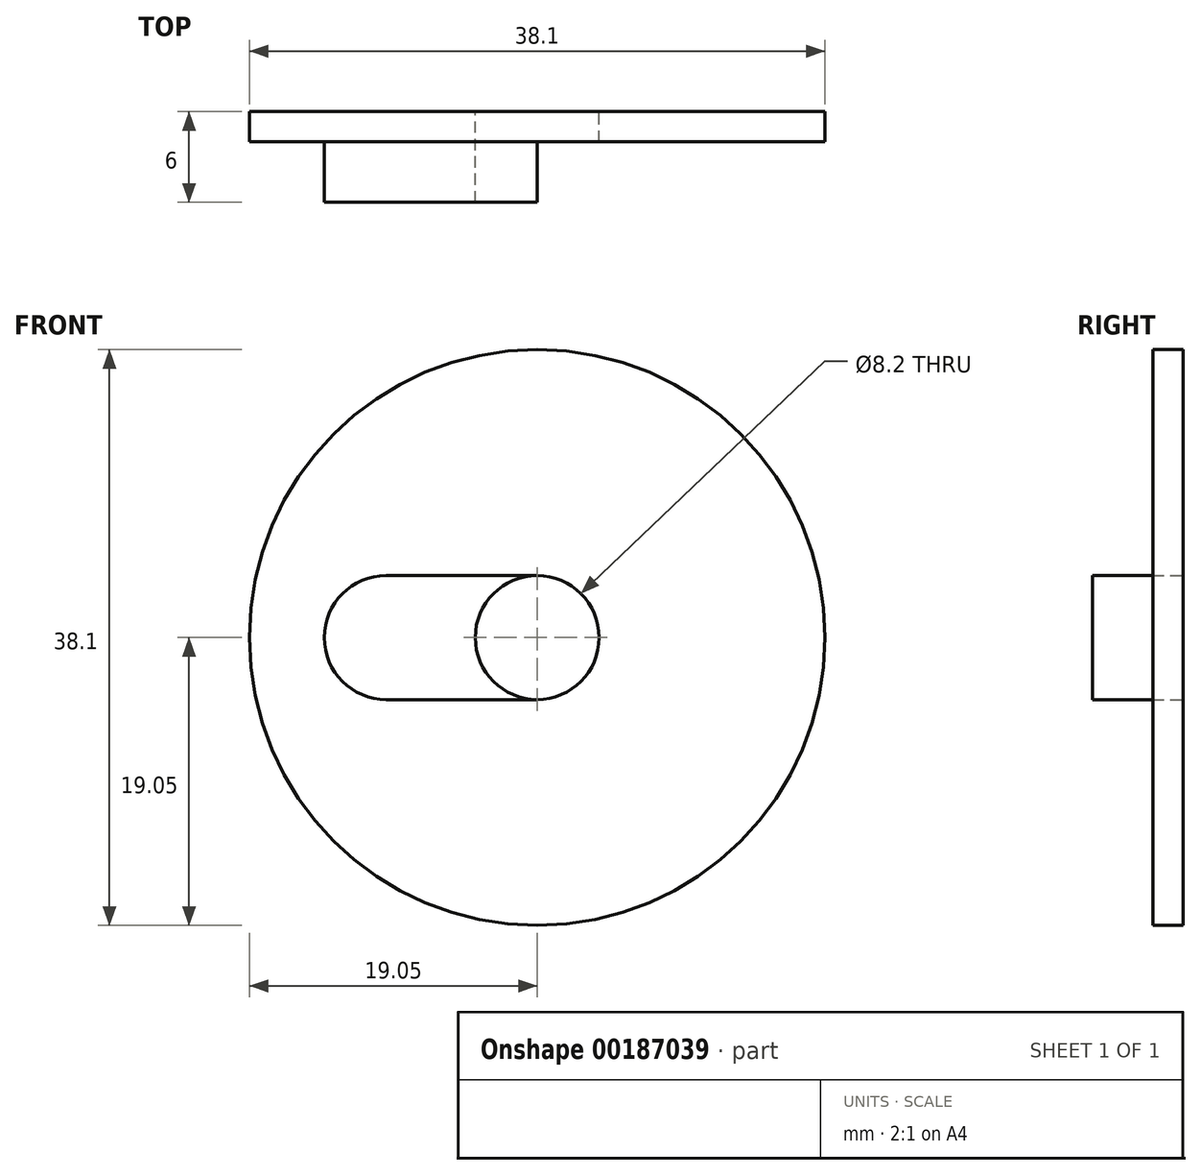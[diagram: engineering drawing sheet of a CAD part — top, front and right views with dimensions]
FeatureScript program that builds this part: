
annotation { "Feature Type Name" : "Feature", "Feature Type Description" : "" }
export const myFeature = defineFeature(function(context is Context, id is Id, definition is map)
    precondition{}
    {
        {
            var Q0;
            Q0=qCreatedBy(makeId("Front.planeOp"),FACE);
            var sketch = newSketch(context, id + "F0", { "sketchPlane" : qUnion([Q0])});
            skCircle(sketch, "E0", {"center": v(0, 0) * mm, "radius": 4.1 * mm});
            skCircle(sketch, "E1", {"center": v(0, 0) * mm, "radius": 19.05 * mm});
            skSolve(sketch);
        }
        {
            var Q0;
            Q0 = qSketchRegion(id + "F0", true);
            extrude(context, id + "F1", {"entities" : qUnion([Q0]), "depth" : 2 * mm});
        }
        {
            var Q0;
            Q0=makeQuery(id+"F1.opExtrude","CAP_FACE",FACE,{"disambiguationData":[OSD([sQuery(id+"F0.wireOp",EDGE,"E0"),sQuery(id+"F0.wireOp",EDGE,"E1")])],"isStart":false});
            var sketch = newSketch(context, id + "F2", { "sketchPlane" : qUnion([Q0])});
            skLineSegment(sketch, "E2", {"start": v(0, -4.1) * mm, "end": v(-10, -4.1) * mm});
            skArc(sketch, "E3", {"start": v(-10, 4.1) * mm, "mid": v(-14.1, 0) * mm, "end": v(-10, -4.1) * mm});
            skLineSegment(sketch, "E4", {"start": v(-10, 4.1) * mm, "end": v(0, 4.1) * mm});
            skLineSegment(sketch, "E5", {"start": v(0, -4.1) * mm, "end": v(8, -4.1) * mm});
            skLineSegment(sketch, "E6", {"start": v(0, 4.1) * mm, "end": v(8, 4.1) * mm});
            skArc(sketch, "E7", {"start": v(8, -4.1) * mm, "mid": v(12.1, 0) * mm, "end": v(8, 4.1) * mm});
            skCircle(sketch, "E8", {"center": v(0, 0) * mm, "radius": 4.1 * mm});
            skSolve(sketch);
        }
        {
            var Q0;
            {var subQ0=sQuery(id+"F2.wireOp",EDGE,"E2");Q0=makeQuery(id+"F2.imprint","IMPRINT",FACE,{"disambiguationData":[TD([[makeQuery(id+"F2.imprint","IMPRINT",EDGE,{"derivedFrom":subQ0}),-1.0]])]});}
            extrude(context, id + "F3", {"entities" : qUnion([Q0]), "operationType" : NewBodyOperationType.ADD, "depth" : 4 * mm});
        }
    });
